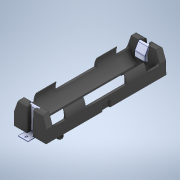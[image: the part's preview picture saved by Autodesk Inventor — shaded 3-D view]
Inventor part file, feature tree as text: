
AUTODESK INVENTOR PART (.ipt)
format: ipt  version: 2020.2 (Build 242310000, 310)  size: 376,320 bytes
history: native  units: in
note: dims shown in document units (in); Inventor stores cm internally (conversion verified against a paired STEP export)
features: other x3, fillet x1
ambient origin geometry x8: Origin, YZ Plane, XZ Plane, XY Plane, X Axis, Y Axis, Z Axis, Center Point
bodies: Volumenkörper1 (feature_tree), Volumenkörper2 (feature_tree), Volumenkörper3 (feature_tree)
feature tree (4):
  other  "1042.stp"
  parser-record x1  (decoder bookkeeping rows leaked as tree rows — omitted from the tree; the rows remain in map.json)
  fillet  "Fillet6"  [1 undecoded]
  other  "Cut-Extrude11[1]"
note: 1 required parameter value undecoded (feature->parameter linkage not recoverable at this tier; creation-order binding heuristic only, values carry confidence <= 0.55)
